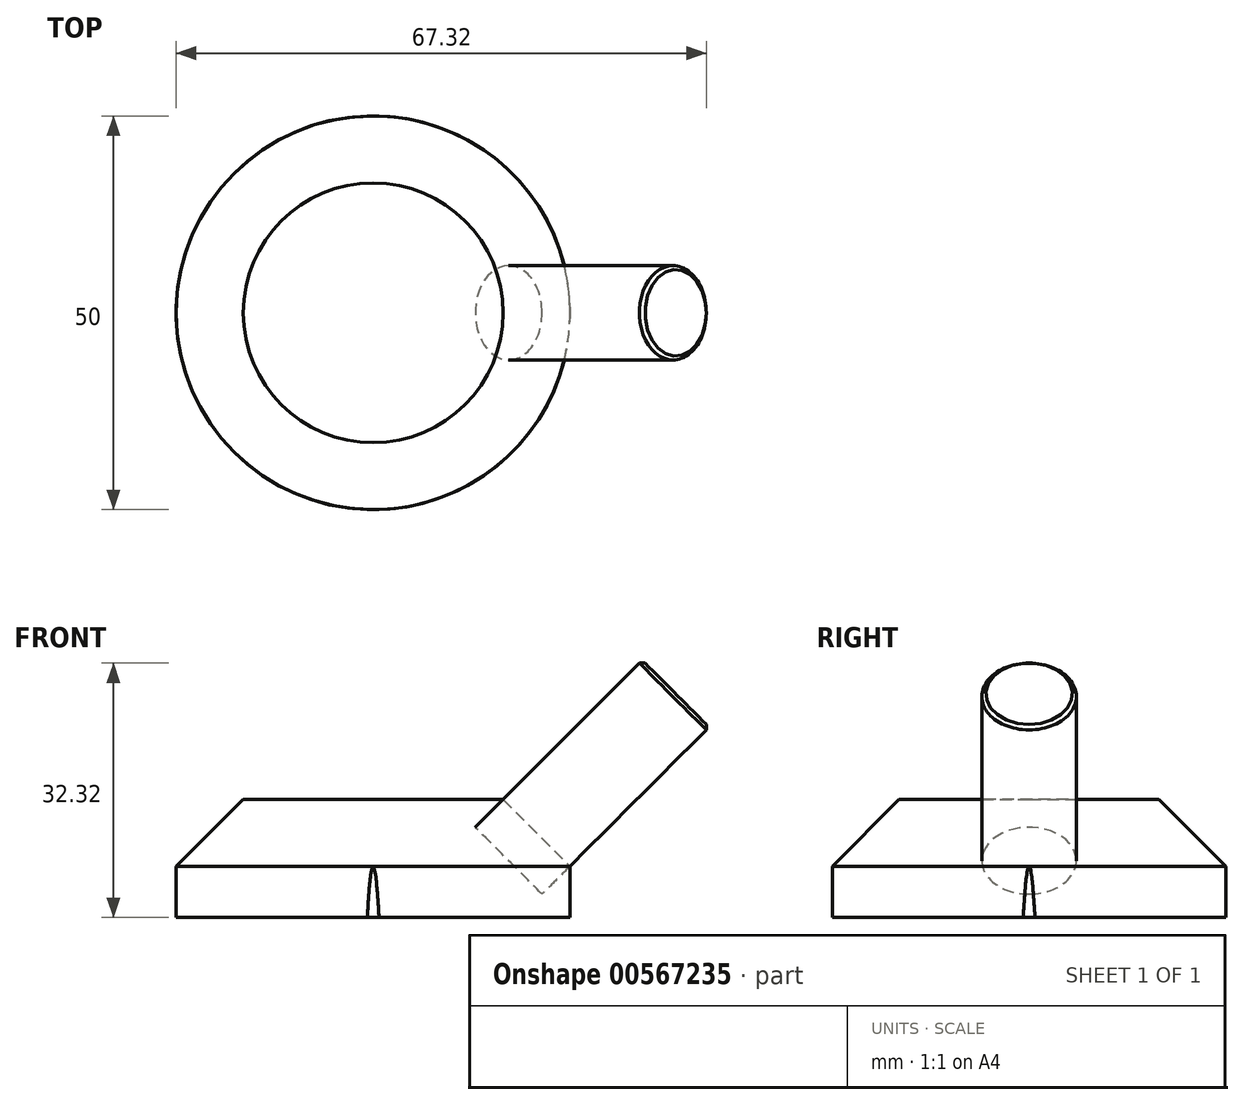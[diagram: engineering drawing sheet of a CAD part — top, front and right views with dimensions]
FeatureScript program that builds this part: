
annotation { "Feature Type Name" : "Feature", "Feature Type Description" : "" }
export const myFeature = defineFeature(function(context is Context, id is Id, definition is map)
    precondition{}
    {
        {
            var Q0;
            Q0=qCreatedBy(makeId("Top.planeOp"),FACE);
            var sketch = newSketch(context, id + "F0", { "sketchPlane" : qUnion([Q0])});
            skLineSegment(sketch, "E0.bottom", {"start": v(-25, 25) * mm, "end": v(25, 25) * mm});
            skLineSegment(sketch, "E0.top", {"start": v(-25, -25) * mm, "end": v(25, -25) * mm});
            skLineSegment(sketch, "E0.left", {"start": v(-25, 25) * mm, "end": v(-25, -25) * mm});
            skLineSegment(sketch, "E0.right", {"start": v(25, 25) * mm, "end": v(25, -25) * mm});
            skSolve(sketch);
        }
        {
            var Q0;
            Q0=qSketchRegion(id+"F0",true);
            extrude(context, id + "F1", {"entities" : qUnion([Q0]), "oppositeDirection" : true, "depth" : 15 * mm, "offsetDistance" : 25 * mm});
        }
        {
            var Q0;
            Q0=makeQuery(id+"F1.opExtrude","CAP_EDGE",EDGE,{"disambiguationData":[OSD([sQuery(id+"F0.wireOp",EDGE,"EIGbn9o8-BXwo-Xmxg-VTVW-IYnVgfDgFz95")])],"isStart":true});
            var Q1;
            Q1=makeQuery(id+"F1.opExtrude","CAP_EDGE",EDGE,{"disambiguationData":[OSD([sQuery(id+"F0.wireOp",EDGE,"E0.right")])],"isStart":true});
            chamfer(context, id + "F2", {"entities" : qUnion([Q0, Q1]), "width" : 8.5 * mm, "tangentPropagation" : true});
        }
        {
            var Q0;
            Q0=makeQuery(id+"F2.opChamfer","BLEND_FACE",FACE,{"disambiguationData":[OSD([sQuery(id+"F0.wireOp",EDGE,"E0.right")])]});
            var sketch = newSketch(context, id + "F3", { "sketchPlane" : qUnion([Q0])});
            skLineSegment(sketch, "E1", {"start": v(0, -11.67) * mm, "end": v(0, -23.69) * mm, "construction": true});
            skCircle(sketch, "E2", {"center": v(0, -17.68) * mm, "radius": 6 * mm});
            skSolve(sketch);
        }
        {
            var Q0;
            Q0=qCreatedBy(makeId("Front.planeOp"),FACE);
            var sketch = newSketch(context, id + "F4", { "sketchPlane" : qUnion([Q0])});
            skPoint(sketch, "E3.0", {"position": v(16.5, 0) * mm});
            skPoint(sketch, "E4.0", {"position": v(25, -8.5) * mm});
            skLineSegment(sketch, "E5", {"start": v(25, -8.5) * mm, "end": v(16.5, 0) * mm});
            skLineSegment(sketch, "E6", {"start": v(0, 0) * mm, "end": v(0, -8.5) * mm});
            skLineSegment(sketch, "E7", {"start": v(57.64, 0) * mm, "end": v(16.5, 0) * mm});
            skLineSegment(sketch, "E8", {"start": v(57.64, 0) * mm, "end": v(57.64, -15) * mm});
            skLineSegment(sketch, "E9", {"start": v(57.64, -15) * mm, "end": v(25.01, -15) * mm});
            skLineSegment(sketch, "E10", {"start": v(25.01, -15) * mm, "end": v(25, -8.5) * mm});
            skSolve(sketch);
        }
        {
            var Q0;
            Q0=makeQuery(id+"F4.imprint","IMPRINT",FACE,{"disambiguationData":[TD([[makeQuery(id+"F4.imprint","IMPRINT",EDGE,{"derivedFrom":sQuery(id+"F4.wireOp",EDGE,"E5")}),-1.0]])]});
            var Q1;
            Q1=sQuery(id+"F4.wireOp",EDGE,"E6");
            revolve(context, id + "F5", {"operationType" : NewBodyOperationType.REMOVE, "entities" : qUnion([Q0]), "axis" : qUnion([Q1]), "revolveType" : RevolveType.ONE_DIRECTION, "angle" : 360 * degree});
        }
        {
            var Q0;
            Q0 = qSketchRegion(id + "F3", true);
            extrude(context, id + "F6", {"entities" : qUnion([Q0]), "depth" : 25 * mm, "offsetDistance" : 25 * mm, "hasSecondDirection" : true, "secondDirectionOppositeDirection" : true, "secondDirectionDepth" : 5 * mm});
        }
        {
            var Q0;
            Q0=makeQuery(id+"F6.opExtrude","CAP_EDGE",EDGE,{"disambiguationData":[OSD([sQuery(id+"F3.wireOp",EDGE,"E2")])],"isStart":false});
            var Q1;
            Q1=makeQuery(id+"F5.boolean.opBoolean","COPY",EDGE,{"derivedFrom":makeQuery(id+"F5.opRevolve","SWEPT_EDGE",EDGE,{"disambiguationData":[OSD([sQuery(id+"F4.wireOp",EDGE,"E5"),sQuery(id+"F4.wireOp",EDGE,"E7")])]})});
            chamfer(context, id + "F7", {"entities" : qUnion([Q0, Q1]), "width" : .5 * mm, "tangentPropagation" : true});
        }
    });
